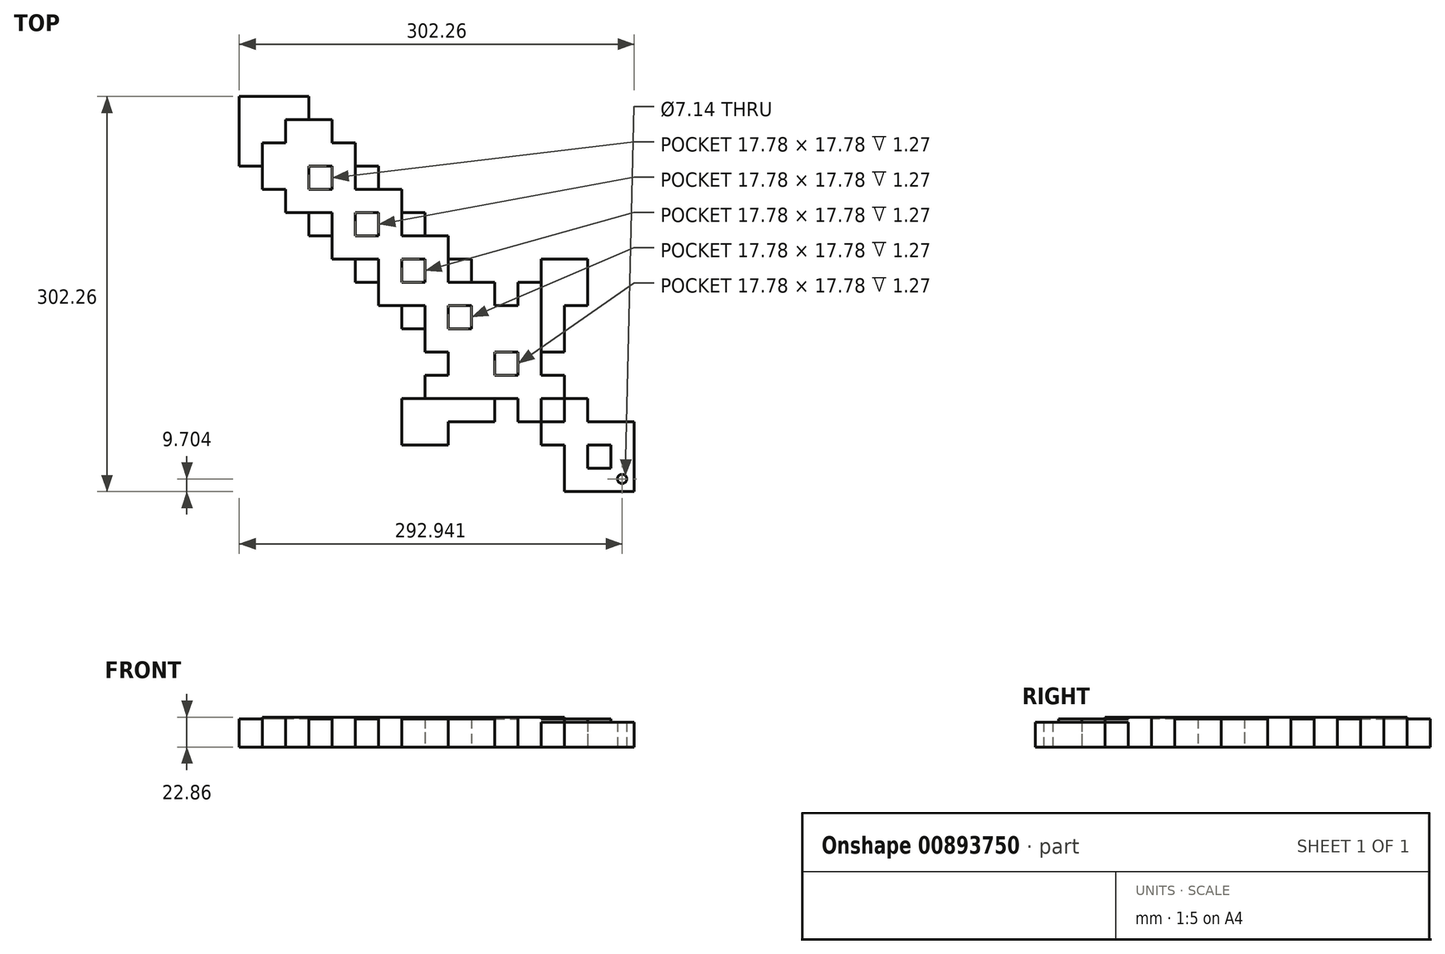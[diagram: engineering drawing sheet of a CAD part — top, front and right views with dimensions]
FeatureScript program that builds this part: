
annotation { "Feature Type Name" : "Feature", "Feature Type Description" : "" }
export const myFeature = defineFeature(function(context is Context, id is Id, definition is map)
    precondition{}
    {
        {
            var Q0;
            Q0=qCreatedBy(makeId("Top.planeOp"),FACE);
            var sketch = newSketch(context, id + "F0", { "sketchPlane" : qUnion([Q0])});
            skLineSegment(sketch, "E0.bottom", {"start": v(7.49, 0) * mm, "end": v(60.83, 0) * mm});
            skLineSegment(sketch, "E0.top", {"start": v(7.49, -53.34) * mm, "end": v(60.83, -53.34) * mm});
            skLineSegment(sketch, "E0.left", {"start": v(7.49, 0) * mm, "end": v(7.49, -53.34) * mm});
            skLineSegment(sketch, "E0.right", {"start": v(60.83, 0) * mm, "end": v(60.83, -53.34) * mm});
            skLineSegment(sketch, "E1.bottom", {"start": v(25.27, -17.78) * mm, "end": v(43.05, -17.78) * mm});
            skLineSegment(sketch, "E1.top", {"start": v(25.27, -35.56) * mm, "end": v(43.05, -35.56) * mm});
            skLineSegment(sketch, "E1.left", {"start": v(25.27, -17.78) * mm, "end": v(25.27, -35.56) * mm});
            skLineSegment(sketch, "E1.right", {"start": v(43.05, -17.78) * mm, "end": v(43.05, -35.56) * mm});
            skLineSegment(sketch, "E2.bottom", {"start": v(-10.3, 17.78) * mm, "end": v(25.27, 17.78) * mm});
            skLineSegment(sketch, "E2.top", {"start": v(-10.3, -17.78) * mm, "end": v(7.49, -17.78) * mm});
            skLineSegment(sketch, "E2.left", {"start": v(-10.3, 17.78) * mm, "end": v(-10.3, -17.78) * mm});
            skLineSegment(sketch, "E2.right", {"start": v(25.27, 17.78) * mm, "end": v(25.27, 0) * mm});
            skLineSegment(sketch, "E3.bottom", {"start": v(-10.3, 0) * mm, "end": v(-28.07, 0) * mm});
            skLineSegment(sketch, "E3.top", {"start": v(7.49, 35.56) * mm, "end": v(-28.07, 35.56) * mm});
            skLineSegment(sketch, "E3.left", {"start": v(7.49, 17.78) * mm, "end": v(7.49, 35.56) * mm});
            skLineSegment(sketch, "E3.right", {"start": v(-28.07, 0) * mm, "end": v(-28.07, 35.56) * mm});
            skLineSegment(sketch, "E4.bottom", {"start": v(-28.07, 17.78) * mm, "end": v(-45.85, 17.78) * mm});
            skLineSegment(sketch, "E4.top", {"start": v(-10.3, 53.34) * mm, "end": v(-45.85, 53.34) * mm});
            skLineSegment(sketch, "E4.left", {"start": v(-10.3, 35.56) * mm, "end": v(-10.3, 53.34) * mm});
            skLineSegment(sketch, "E4.right", {"start": v(-45.85, 17.78) * mm, "end": v(-45.85, 53.34) * mm});
            skLineSegment(sketch, "E5.bottom", {"start": v(-45.85, 53.34) * mm, "end": v(-10.3, 53.34) * mm});
            skLineSegment(sketch, "E5.top", {"start": v(-45.85, 88.9) * mm, "end": v(-10.3, 88.9) * mm});
            skLineSegment(sketch, "E5.left", {"start": v(-45.85, 53.34) * mm, "end": v(-45.85, 88.9) * mm});
            skLineSegment(sketch, "E5.right", {"start": v(-10.3, 53.34) * mm, "end": v(-10.3, 88.9) * mm});
            skPoint(sketch, "E6.oppositeSnap0", {"position": v(-36.96, 17.78) * mm});
            skLineSegment(sketch, "E6.bottom", {"start": v(-45.85, 53.34) * mm, "end": v(-81.41, 53.34) * mm});
            skLineSegment(sketch, "E6.top", {"start": v(-45.85, 17.78) * mm, "end": v(-81.41, 17.78) * mm});
            skLineSegment(sketch, "E6.left", {"start": v(-45.85, 53.34) * mm, "end": v(-45.85, 17.78) * mm});
            skLineSegment(sketch, "E6.right", {"start": v(-81.41, 53.34) * mm, "end": v(-81.41, 17.78) * mm});
            skLineSegment(sketch, "E7.bottom", {"start": v(-10.3, 88.9) * mm, "end": v(7.49, 88.9) * mm});
            skLineSegment(sketch, "E7.top", {"start": v(-10.3, 53.34) * mm, "end": v(7.49, 53.34) * mm});
            skLineSegment(sketch, "E7.left", {"start": v(-10.3, 88.9) * mm, "end": v(-10.3, 53.34) * mm});
            skLineSegment(sketch, "E7.right", {"start": v(7.49, 88.9) * mm, "end": v(7.49, 53.34) * mm});
            skLineSegment(sketch, "E8.right", {"start": v(-10.3, 88.9) * mm, "end": v(-10.3, 106.7) * mm});
            skLineSegment(sketch, "E9.bottom", {"start": v(-81.41, 17.78) * mm, "end": v(-99.41, 17.78) * mm});
            skLineSegment(sketch, "E9.left", {"start": v(-81.41, 17.78) * mm, "end": v(-81.41, 53.34) * mm});
            skLineSegment(sketch, "E10.bottom", {"start": v(-81.41, 17.78) * mm, "end": v(-45.85, 17.78) * mm});
            skLineSegment(sketch, "E10.top", {"start": v(-81.41, 0) * mm, "end": v(-45.85, 0) * mm});
            skLineSegment(sketch, "E10.left", {"start": v(-81.41, 17.78) * mm, "end": v(-81.41, 0) * mm});
            skLineSegment(sketch, "E10.right", {"start": v(-45.85, 17.78) * mm, "end": v(-45.85, 0) * mm});
            skLineSegment(sketch, "E11.bottom", {"start": v(-81.41, 17.78) * mm, "end": v(-116.97, 17.78) * mm});
            skLineSegment(sketch, "E11.top", {"start": v(-81.41, -17.78) * mm, "end": v(-116.97, -17.78) * mm});
            skLineSegment(sketch, "E11.left", {"start": v(-81.41, 17.78) * mm, "end": v(-81.41, -17.78) * mm});
            skLineSegment(sketch, "E11.right", {"start": v(-116.97, 17.78) * mm, "end": v(-116.97, -17.78) * mm});
            skLineSegment(sketch, "E12.bottom", {"start": v(-10.3, 88.9) * mm, "end": v(25.27, 88.9) * mm});
            skLineSegment(sketch, "E12.top", {"start": v(-10.3, 124.46) * mm, "end": v(25.27, 124.46) * mm});
            skLineSegment(sketch, "E12.left", {"start": v(-10.3, 88.9) * mm, "end": v(-10.3, 124.46) * mm});
            skLineSegment(sketch, "E12.right", {"start": v(25.27, 88.9) * mm, "end": v(25.27, 124.46) * mm});
            skLineSegment(sketch, "E13.top", {"start": v(-45.85, 88.9) * mm, "end": v(-81.41, 88.9) * mm});
            skLineSegment(sketch, "E13.right", {"start": v(-81.41, 53.34) * mm, "end": v(-81.41, 88.9) * mm});
            skPoint(sketch, "E14.end.orphan", {"position": v(-28.07, 88.9) * mm});
            skPoint(sketch, "E8.top.start.orphan", {"position": v(-28.3, 106.68) * mm});
            skPoint(sketch, "E15.end.orphan", {"position": v(-81.41, 35.56) * mm});
            skPoint(sketch, "E9.right.end.orphan", {"position": v(-99.41, 35.56) * mm});
            skLineSegment(sketch, "E16.bottom", {"start": v(-28.3, 106.68) * mm, "end": v(-10.3, 106.68) * mm});
            skLineSegment(sketch, "E16.top", {"start": v(-28.3, 88.9) * mm, "end": v(-10.3, 88.9) * mm});
            skLineSegment(sketch, "E16.left", {"start": v(-28.3, 106.68) * mm, "end": v(-28.3, 88.9) * mm});
            skLineSegment(sketch, "E16.right", {"start": v(-10.3, 106.68) * mm, "end": v(-10.3, 88.9) * mm});
            skLineSegment(sketch, "E17.bottom", {"start": v(-99.41, 35.56) * mm, "end": v(-81.41, 35.56) * mm});
            skLineSegment(sketch, "E17.top", {"start": v(-99.41, 17.78) * mm, "end": v(-81.41, 17.78) * mm});
            skLineSegment(sketch, "E17.left", {"start": v(-99.41, 35.56) * mm, "end": v(-99.41, 17.78) * mm});
            skLineSegment(sketch, "E17.right", {"start": v(-81.41, 35.56) * mm, "end": v(-81.41, 17.78) * mm});
            skLineSegment(sketch, "E18.bottom", {"start": v(-63.63, 71.12) * mm, "end": v(-99.2, 71.12) * mm});
            skLineSegment(sketch, "E18.top", {"start": v(-63.63, 106.68) * mm, "end": v(-99.2, 106.68) * mm});
            skLineSegment(sketch, "E18.left", {"start": v(-63.63, 71.12) * mm, "end": v(-63.63, 106.68) * mm});
            skLineSegment(sketch, "E18.right", {"start": v(-99.2, 71.12) * mm, "end": v(-99.2, 106.68) * mm});
            skLineSegment(sketch, "E19.bottom", {"start": v(-99.2, 88.9) * mm, "end": v(-116.97, 88.9) * mm});
            skLineSegment(sketch, "E19.top", {"start": v(-81.41, 124.46) * mm, "end": v(-116.97, 124.46) * mm});
            skLineSegment(sketch, "E19.left", {"start": v(-81.41, 106.68) * mm, "end": v(-81.41, 124.46) * mm});
            skLineSegment(sketch, "E19.right", {"start": v(-116.97, 88.9) * mm, "end": v(-116.97, 124.46) * mm});
            skLineSegment(sketch, "E20.bottom", {"start": v(-116.97, 106.68) * mm, "end": v(-134.75, 106.68) * mm});
            skLineSegment(sketch, "E20.top", {"start": v(-99.2, 142.24) * mm, "end": v(-134.75, 142.24) * mm});
            skLineSegment(sketch, "E20.left", {"start": v(-99.2, 124.46) * mm, "end": v(-99.2, 142.24) * mm});
            skLineSegment(sketch, "E20.right", {"start": v(-134.75, 106.68) * mm, "end": v(-134.75, 142.24) * mm});
            skLineSegment(sketch, "E21.bottom", {"start": v(-134.75, 124.46) * mm, "end": v(-152.53, 124.46) * mm});
            skLineSegment(sketch, "E21.top", {"start": v(-116.97, 160.02) * mm, "end": v(-152.53, 160.02) * mm});
            skLineSegment(sketch, "E21.left", {"start": v(-116.97, 142.24) * mm, "end": v(-116.97, 160.02) * mm});
            skLineSegment(sketch, "E21.right", {"start": v(-152.53, 124.46) * mm, "end": v(-152.53, 160.02) * mm});
            skLineSegment(sketch, "E22.bottom", {"start": v(-152.53, 142.24) * mm, "end": v(-170.31, 142.24) * mm});
            skLineSegment(sketch, "E22.top", {"start": v(-134.75, 177.8) * mm, "end": v(-170.31, 177.8) * mm});
            skLineSegment(sketch, "E22.left", {"start": v(-134.75, 160.02) * mm, "end": v(-134.75, 177.8) * mm});
            skLineSegment(sketch, "E22.right", {"start": v(-170.31, 142.24) * mm, "end": v(-170.31, 177.8) * mm});
            skLineSegment(sketch, "E23.bottom", {"start": v(-170.31, 160.02) * mm, "end": v(-188.1, 160.02) * mm});
            skLineSegment(sketch, "E23.top", {"start": v(-152.53, 195.58) * mm, "end": v(-188.1, 195.58) * mm});
            skLineSegment(sketch, "E23.left", {"start": v(-152.53, 177.8) * mm, "end": v(-152.53, 195.58) * mm});
            skLineSegment(sketch, "E23.right", {"start": v(-188.1, 160.02) * mm, "end": v(-188.1, 195.58) * mm});
            skLineSegment(sketch, "E24.bottom", {"start": v(-188.1, 177.8) * mm, "end": v(-205.87, 177.8) * mm});
            skLineSegment(sketch, "E24.top", {"start": v(-170.31, 213.36) * mm, "end": v(-205.87, 213.36) * mm});
            skLineSegment(sketch, "E24.left", {"start": v(-170.31, 195.58) * mm, "end": v(-170.31, 213.36) * mm});
            skLineSegment(sketch, "E24.right", {"start": v(-205.87, 177.8) * mm, "end": v(-205.87, 213.36) * mm});
            skLineSegment(sketch, "E25.bottom", {"start": v(-205.87, 195.58) * mm, "end": v(-223.65, 195.58) * mm});
            skLineSegment(sketch, "E25.top", {"start": v(-188.1, 231.14) * mm, "end": v(-223.65, 231.14) * mm});
            skLineSegment(sketch, "E25.left", {"start": v(-188.1, 213.36) * mm, "end": v(-188.1, 231.14) * mm});
            skLineSegment(sketch, "E25.right", {"start": v(-223.65, 195.58) * mm, "end": v(-223.65, 231.14) * mm});
            skLineSegment(sketch, "E26.top", {"start": v(-223.65, 195.58) * mm, "end": v(-241.43, 195.58) * mm});
            skLineSegment(sketch, "E26.right", {"start": v(-241.43, 231.14) * mm, "end": v(-241.43, 195.58) * mm});
            skLineSegment(sketch, "E27.top", {"start": v(-188.1, 248.92) * mm, "end": v(-223.65, 248.92) * mm});
            skLineSegment(sketch, "E27.left", {"start": v(-188.1, 231.14) * mm, "end": v(-188.1, 248.92) * mm});
            skLineSegment(sketch, "E28.top", {"start": v(-223.65, 248.92) * mm, "end": v(-241.43, 248.92) * mm});
            skLineSegment(sketch, "E28.right", {"start": v(-241.43, 231.14) * mm, "end": v(-241.43, 248.92) * mm});
            skLineSegment(sketch, "E29.bottom", {"start": v(-63.63, 106.68) * mm, "end": v(-45.85, 106.68) * mm});
            skLineSegment(sketch, "E29.top", {"start": v(-63.63, 88.9) * mm, "end": v(-45.85, 88.9) * mm});
            skLineSegment(sketch, "E29.left", {"start": v(-63.63, 106.68) * mm, "end": v(-63.63, 88.9) * mm});
            skLineSegment(sketch, "E29.right", {"start": v(-45.85, 106.68) * mm, "end": v(-45.85, 88.9) * mm});
            skLineSegment(sketch, "E30.bottom", {"start": v(-99.2, 71.12) * mm, "end": v(-81.41, 71.12) * mm});
            skLineSegment(sketch, "E30.top", {"start": v(-99.2, 53.34) * mm, "end": v(-81.41, 53.34) * mm});
            skLineSegment(sketch, "E30.left", {"start": v(-99.2, 71.12) * mm, "end": v(-99.2, 53.34) * mm});
            skLineSegment(sketch, "E30.right", {"start": v(-81.41, 71.12) * mm, "end": v(-81.41, 53.34) * mm});
            skLineSegment(sketch, "E31.bottom", {"start": v(-223.65, 195.58) * mm, "end": v(-205.87, 195.58) * mm});
            skLineSegment(sketch, "E31.top", {"start": v(-223.65, 177.8) * mm, "end": v(-205.87, 177.8) * mm});
            skLineSegment(sketch, "E31.left", {"start": v(-223.65, 195.58) * mm, "end": v(-223.65, 177.8) * mm});
            skLineSegment(sketch, "E31.right", {"start": v(-205.87, 195.58) * mm, "end": v(-205.87, 177.8) * mm});
            skLineSegment(sketch, "E32.bottom", {"start": v(-205.87, 177.8) * mm, "end": v(-188.1, 177.8) * mm});
            skLineSegment(sketch, "E32.top", {"start": v(-205.87, 160.02) * mm, "end": v(-188.1, 160.02) * mm});
            skLineSegment(sketch, "E32.left", {"start": v(-205.87, 177.8) * mm, "end": v(-205.87, 160.02) * mm});
            skLineSegment(sketch, "E32.right", {"start": v(-188.1, 177.8) * mm, "end": v(-188.1, 160.02) * mm});
            skLineSegment(sketch, "E33.bottom", {"start": v(-188.1, 160.02) * mm, "end": v(-170.31, 160.02) * mm});
            skLineSegment(sketch, "E33.top", {"start": v(-188.1, 142.24) * mm, "end": v(-170.31, 142.24) * mm});
            skLineSegment(sketch, "E33.left", {"start": v(-188.1, 160.02) * mm, "end": v(-188.1, 142.24) * mm});
            skLineSegment(sketch, "E33.right", {"start": v(-170.31, 160.02) * mm, "end": v(-170.31, 142.24) * mm});
            skLineSegment(sketch, "E34.bottom", {"start": v(-170.31, 142.24) * mm, "end": v(-152.53, 142.24) * mm});
            skLineSegment(sketch, "E34.top", {"start": v(-170.31, 124.46) * mm, "end": v(-152.53, 124.46) * mm});
            skLineSegment(sketch, "E34.left", {"start": v(-170.31, 142.24) * mm, "end": v(-170.31, 124.46) * mm});
            skLineSegment(sketch, "E34.right", {"start": v(-152.53, 142.24) * mm, "end": v(-152.53, 124.46) * mm});
            skLineSegment(sketch, "E35.bottom", {"start": v(-152.53, 124.46) * mm, "end": v(-134.75, 124.46) * mm});
            skLineSegment(sketch, "E35.top", {"start": v(-152.53, 106.68) * mm, "end": v(-134.75, 106.68) * mm});
            skLineSegment(sketch, "E35.left", {"start": v(-152.53, 124.46) * mm, "end": v(-152.53, 106.68) * mm});
            skLineSegment(sketch, "E35.right", {"start": v(-134.75, 124.46) * mm, "end": v(-134.75, 106.68) * mm});
            skLineSegment(sketch, "E36.bottom", {"start": v(-134.75, 106.68) * mm, "end": v(-116.97, 106.68) * mm});
            skLineSegment(sketch, "E36.top", {"start": v(-134.75, 88.9) * mm, "end": v(-116.97, 88.9) * mm});
            skLineSegment(sketch, "E36.left", {"start": v(-134.75, 106.68) * mm, "end": v(-134.75, 88.9) * mm});
            skLineSegment(sketch, "E36.right", {"start": v(-116.97, 106.68) * mm, "end": v(-116.97, 88.9) * mm});
            skLineSegment(sketch, "E37.bottom", {"start": v(-116.97, 88.9) * mm, "end": v(-99.2, 88.9) * mm});
            skLineSegment(sketch, "E37.top", {"start": v(-116.97, 71.12) * mm, "end": v(-99.2, 71.12) * mm});
            skLineSegment(sketch, "E37.left", {"start": v(-116.97, 88.9) * mm, "end": v(-116.97, 71.12) * mm});
            skLineSegment(sketch, "E37.right", {"start": v(-99.2, 88.9) * mm, "end": v(-99.2, 71.12) * mm});
            skLineSegment(sketch, "E38.bottom", {"start": v(-188.1, 231.14) * mm, "end": v(-170.31, 231.14) * mm});
            skLineSegment(sketch, "E38.top", {"start": v(-188.1, 213.36) * mm, "end": v(-170.31, 213.36) * mm});
            skLineSegment(sketch, "E38.left", {"start": v(-188.1, 231.14) * mm, "end": v(-188.1, 213.36) * mm});
            skLineSegment(sketch, "E38.right", {"start": v(-170.31, 231.14) * mm, "end": v(-170.31, 213.36) * mm});
            skLineSegment(sketch, "E39.bottom", {"start": v(-170.31, 213.36) * mm, "end": v(-152.53, 213.36) * mm});
            skLineSegment(sketch, "E39.top", {"start": v(-170.31, 195.58) * mm, "end": v(-152.53, 195.58) * mm});
            skLineSegment(sketch, "E39.left", {"start": v(-170.31, 213.36) * mm, "end": v(-170.31, 195.58) * mm});
            skLineSegment(sketch, "E39.right", {"start": v(-152.53, 213.36) * mm, "end": v(-152.53, 195.58) * mm});
            skLineSegment(sketch, "E40.bottom", {"start": v(-152.53, 195.58) * mm, "end": v(-134.75, 195.58) * mm});
            skLineSegment(sketch, "E40.top", {"start": v(-152.53, 177.8) * mm, "end": v(-134.75, 177.8) * mm});
            skLineSegment(sketch, "E40.left", {"start": v(-152.53, 195.58) * mm, "end": v(-152.53, 177.8) * mm});
            skLineSegment(sketch, "E40.right", {"start": v(-134.75, 195.58) * mm, "end": v(-134.75, 177.8) * mm});
            skLineSegment(sketch, "E41.bottom", {"start": v(-134.75, 177.8) * mm, "end": v(-116.97, 177.8) * mm});
            skLineSegment(sketch, "E41.top", {"start": v(-134.75, 160.02) * mm, "end": v(-116.97, 160.02) * mm});
            skLineSegment(sketch, "E41.left", {"start": v(-134.75, 177.8) * mm, "end": v(-134.75, 160.02) * mm});
            skLineSegment(sketch, "E41.right", {"start": v(-116.97, 177.8) * mm, "end": v(-116.97, 160.02) * mm});
            skLineSegment(sketch, "E42.bottom", {"start": v(-116.97, 160.02) * mm, "end": v(-99.2, 160.02) * mm});
            skLineSegment(sketch, "E42.top", {"start": v(-116.97, 142.24) * mm, "end": v(-99.2, 142.24) * mm});
            skLineSegment(sketch, "E42.left", {"start": v(-116.97, 160.02) * mm, "end": v(-116.97, 142.24) * mm});
            skLineSegment(sketch, "E42.right", {"start": v(-99.2, 160.02) * mm, "end": v(-99.2, 142.24) * mm});
            skLineSegment(sketch, "E43.bottom", {"start": v(-99.2, 142.24) * mm, "end": v(-81.41, 142.24) * mm});
            skLineSegment(sketch, "E43.top", {"start": v(-99.2, 124.46) * mm, "end": v(-81.41, 124.46) * mm});
            skLineSegment(sketch, "E43.left", {"start": v(-99.2, 142.24) * mm, "end": v(-99.2, 124.46) * mm});
            skLineSegment(sketch, "E43.right", {"start": v(-81.41, 142.24) * mm, "end": v(-81.41, 124.46) * mm});
            skLineSegment(sketch, "E44.bottom", {"start": v(-81.41, 124.46) * mm, "end": v(-63.63, 124.46) * mm});
            skLineSegment(sketch, "E44.top", {"start": v(-81.41, 106.68) * mm, "end": v(-63.63, 106.68) * mm});
            skLineSegment(sketch, "E44.left", {"start": v(-81.41, 124.46) * mm, "end": v(-81.41, 106.68) * mm});
            skLineSegment(sketch, "E44.right", {"start": v(-63.63, 124.46) * mm, "end": v(-63.63, 106.68) * mm});
            skLineSegment(sketch, "E45.top", {"start": v(-99.41, 0) * mm, "end": v(-81.41, 0) * mm});
            skLineSegment(sketch, "E45.left", {"start": v(-99.41, 17.78) * mm, "end": v(-99.41, 0) * mm});
            skLineSegment(sketch, "E46.bottom", {"start": v(-10.3, 106.7) * mm, "end": v(7.49, 106.7) * mm});
            skLineSegment(sketch, "E46.left", {"start": v(-10.3, 106.7) * mm, "end": v(-10.3, 88.9) * mm});
            skLineSegment(sketch, "E46.right", {"start": v(7.49, 106.7) * mm, "end": v(7.49, 88.9) * mm});
            skLineSegment(sketch, "E47.top", {"start": v(-81.41, 35.56) * mm, "end": v(-45.85, 35.56) * mm});
            skLineSegment(sketch, "E47.left", {"start": v(-81.41, 17.78) * mm, "end": v(-81.41, 35.56) * mm});
            skLineSegment(sketch, "E47.right", {"start": v(-45.85, 17.78) * mm, "end": v(-45.85, 35.56) * mm});
            skLineSegment(sketch, "E48.bottom", {"start": v(-28.07, 88.9) * mm, "end": v(-10.3, 88.9) * mm});
            skLineSegment(sketch, "E48.top", {"start": v(-28.07, 53.34) * mm, "end": v(-10.3, 53.34) * mm});
            skLineSegment(sketch, "E48.left", {"start": v(-28.07, 88.9) * mm, "end": v(-28.07, 53.34) * mm});
            skLineSegment(sketch, "E49.bottom", {"start": v(-45.85, 53.34) * mm, "end": v(-28.07, 53.34) * mm});
            skLineSegment(sketch, "E49.top", {"start": v(-45.85, 35.56) * mm, "end": v(-28.07, 35.56) * mm});
            skLineSegment(sketch, "E49.left", {"start": v(-45.85, 53.34) * mm, "end": v(-45.85, 35.56) * mm});
            skLineSegment(sketch, "E49.right", {"start": v(-28.07, 53.34) * mm, "end": v(-28.07, 35.56) * mm});
            skLineSegment(sketch, "E50.bottom", {"start": v(25.27, -17.78) * mm, "end": v(7.49, -17.78) * mm});
            skLineSegment(sketch, "E50.top", {"start": v(25.27, 0) * mm, "end": v(7.49, 0) * mm});
            skLineSegment(sketch, "E50.left", {"start": v(25.27, -17.78) * mm, "end": v(25.27, 0) * mm});
            skLineSegment(sketch, "E50.right", {"start": v(7.49, -17.78) * mm, "end": v(7.49, 0) * mm});
            skLineSegment(sketch, "E51.bottom", {"start": v(7.49, 0) * mm, "end": v(-10.3, 0) * mm});
            skLineSegment(sketch, "E51.top", {"start": v(7.49, 17.78) * mm, "end": v(-10.3, 17.78) * mm});
            skLineSegment(sketch, "E51.left", {"start": v(7.49, 0) * mm, "end": v(7.49, 17.78) * mm});
            skLineSegment(sketch, "E51.right", {"start": v(-10.3, 0) * mm, "end": v(-10.3, 17.78) * mm});
            skLineSegment(sketch, "E52.bottom", {"start": v(-10.14, 17.95) * mm, "end": v(-28.07, 17.95) * mm});
            skLineSegment(sketch, "E52.top", {"start": v(-10.14, 35.56) * mm, "end": v(-28.07, 35.56) * mm});
            skLineSegment(sketch, "E52.left", {"start": v(-10.14, 17.95) * mm, "end": v(-10.14, 35.56) * mm});
            skLineSegment(sketch, "E52.right", {"start": v(-28.07, 17.95) * mm, "end": v(-28.07, 35.56) * mm});
            skLineSegment(sketch, "E53.bottom", {"start": v(-45.85, 53.34) * mm, "end": v(-63.63, 53.34) * mm});
            skLineSegment(sketch, "E53.top", {"start": v(-45.85, 71.12) * mm, "end": v(-63.63, 71.12) * mm});
            skLineSegment(sketch, "E53.left", {"start": v(-45.85, 53.34) * mm, "end": v(-45.85, 71.12) * mm});
            skLineSegment(sketch, "E53.right", {"start": v(-63.63, 53.34) * mm, "end": v(-63.63, 71.12) * mm});
            skLineSegment(sketch, "E54.bottom", {"start": v(-81.41, 88.9) * mm, "end": v(-99.2, 88.9) * mm});
            skLineSegment(sketch, "E54.top", {"start": v(-81.41, 106.68) * mm, "end": v(-99.2, 106.68) * mm});
            skLineSegment(sketch, "E54.left", {"start": v(-81.41, 88.9) * mm, "end": v(-81.41, 106.68) * mm});
            skLineSegment(sketch, "E54.right", {"start": v(-99.2, 88.9) * mm, "end": v(-99.2, 106.68) * mm});
            skLineSegment(sketch, "E55.bottom", {"start": v(-99.2, 106.68) * mm, "end": v(-116.97, 106.68) * mm});
            skLineSegment(sketch, "E55.top", {"start": v(-99.2, 124.46) * mm, "end": v(-116.97, 124.46) * mm});
            skLineSegment(sketch, "E55.left", {"start": v(-99.2, 106.68) * mm, "end": v(-99.2, 124.46) * mm});
            skLineSegment(sketch, "E55.right", {"start": v(-116.97, 106.68) * mm, "end": v(-116.97, 124.46) * mm});
            skLineSegment(sketch, "E56.bottom", {"start": v(-117.55, 124.26) * mm, "end": v(-134.75, 124.26) * mm});
            skLineSegment(sketch, "E56.top", {"start": v(-117.55, 142.24) * mm, "end": v(-134.75, 142.24) * mm});
            skLineSegment(sketch, "E56.left", {"start": v(-117.55, 124.26) * mm, "end": v(-117.55, 142.24) * mm});
            skLineSegment(sketch, "E56.right", {"start": v(-134.75, 124.26) * mm, "end": v(-134.75, 142.24) * mm});
            skLineSegment(sketch, "E57.bottom", {"start": v(-134.75, 142.24) * mm, "end": v(-152.53, 142.24) * mm});
            skLineSegment(sketch, "E57.top", {"start": v(-134.75, 160.02) * mm, "end": v(-152.53, 160.02) * mm});
            skLineSegment(sketch, "E57.left", {"start": v(-134.75, 142.24) * mm, "end": v(-134.75, 160.02) * mm});
            skLineSegment(sketch, "E57.right", {"start": v(-152.53, 142.24) * mm, "end": v(-152.53, 160.02) * mm});
            skLineSegment(sketch, "E58.bottom", {"start": v(-152.53, 160.02) * mm, "end": v(-170.31, 160.02) * mm});
            skLineSegment(sketch, "E58.top", {"start": v(-152.53, 177.8) * mm, "end": v(-170.31, 177.8) * mm});
            skLineSegment(sketch, "E58.left", {"start": v(-152.53, 160.02) * mm, "end": v(-152.53, 177.8) * mm});
            skLineSegment(sketch, "E58.right", {"start": v(-170.31, 160.02) * mm, "end": v(-170.31, 177.8) * mm});
            skLineSegment(sketch, "E59.bottom", {"start": v(-170.31, 177.8) * mm, "end": v(-188.1, 177.8) * mm});
            skLineSegment(sketch, "E59.top", {"start": v(-170.31, 195.58) * mm, "end": v(-188.1, 195.58) * mm});
            skLineSegment(sketch, "E59.left", {"start": v(-170.31, 177.8) * mm, "end": v(-170.31, 195.58) * mm});
            skLineSegment(sketch, "E59.right", {"start": v(-188.1, 177.8) * mm, "end": v(-188.1, 195.58) * mm});
            skLineSegment(sketch, "E60.bottom", {"start": v(-188.1, 195.58) * mm, "end": v(-205.87, 195.58) * mm});
            skLineSegment(sketch, "E60.top", {"start": v(-188.1, 213.36) * mm, "end": v(-205.87, 213.36) * mm});
            skLineSegment(sketch, "E60.left", {"start": v(-188.1, 195.58) * mm, "end": v(-188.1, 213.36) * mm});
            skLineSegment(sketch, "E60.right", {"start": v(-205.87, 195.58) * mm, "end": v(-205.87, 213.36) * mm});
            skLineSegment(sketch, "E61.bottom", {"start": v(-205.87, 213.36) * mm, "end": v(-223.65, 213.36) * mm});
            skLineSegment(sketch, "E61.top", {"start": v(-205.87, 231.14) * mm, "end": v(-223.65, 231.14) * mm});
            skLineSegment(sketch, "E61.left", {"start": v(-205.87, 213.36) * mm, "end": v(-205.87, 231.14) * mm});
            skLineSegment(sketch, "E61.right", {"start": v(-223.65, 213.36) * mm, "end": v(-223.65, 231.14) * mm});
            skPoint(sketch, "E62", {"position": v(51.51, -43.64) * mm});
            skSolve(sketch);
        }
        {
            var Q0;
            {var subQ0=sQuery(id+"F0.wireOp",EDGE,"E56.bottom");Q0=makeQuery(id+"F0.imprint","IMPRINT",FACE,{"disambiguationData":[TD([[makeQuery(id+"F0.imprint","IMPRINT",EDGE,{"derivedFrom":subQ0}),-1.0]])]});}
            var Q1;
            {var subQ2=sQuery(id+"F0.wireOp",EDGE,"E22.bottom");Q1=makeQuery(id+"F0.imprint","IMPRINT",FACE,{"disambiguationData":[TD([[makeQuery(id+"F0.imprint","IMPRINT",EDGE,{"derivedFrom":subQ2}),-1.0]])]});}
            var Q2;
            {var subQ0=sQuery(id+"F0.wireOp",EDGE,"E6.top");Q2=makeQuery(id+"F0.imprint","IMPRINT",FACE,{"disambiguationData":[TD([[makeQuery(id+"F0.imprint","IMPRINT",EDGE,{"derivedFrom":subQ0}),-1.0]])]});}
            var Q3;
            {var subQ2=sQuery(id+"F0.wireOp",EDGE,"E23.bottom");Q3=makeQuery(id+"F0.imprint","IMPRINT",FACE,{"disambiguationData":[TD([[makeQuery(id+"F0.imprint","IMPRINT",EDGE,{"derivedFrom":subQ2}),-1.0]])]});}
            var Q4;
            {var subQ2=sQuery(id+"F0.wireOp",EDGE,"E20.left");Q4=makeQuery(id+"F0.imprint","IMPRINT",FACE,{"disambiguationData":[TD([[makeQuery(id+"F0.imprint","IMPRINT",EDGE,{"derivedFrom":subQ2}),-1.0]])]});}
            var Q5;
            {var subQ3=sQuery(id+"F0.wireOp",EDGE,"E7.bottom");Q5=makeQuery(id+"F0.imprint","IMPRINT",FACE,{"disambiguationData":[TD([[makeQuery(id+"F0.imprint","IMPRINT",EDGE,{"derivedFrom":subQ3}),1.0]])]});}
            var Q6;
            {var subQ0=sQuery(id+"F0.wireOp",EDGE,"E54.left");Q6=makeQuery(id+"F0.imprint","IMPRINT",FACE,{"disambiguationData":[TD([[makeQuery(id+"F0.imprint","IMPRINT",EDGE,{"derivedFrom":subQ0}),-1.0]])]});}
            var Q7;
            {var subQ4=sQuery(id+"F0.wireOp",EDGE,"E50.bottom");Q7=makeQuery(id+"F0.imprint","IMPRINT",FACE,{"disambiguationData":[TD([[makeQuery(id+"F0.imprint","IMPRINT",EDGE,{"derivedFrom":subQ4}),-1.0]])]});}
            var Q8;
            {var subQ0=sQuery(id+"F0.wireOp",EDGE,"E9.bottom");Q8=makeQuery(id+"F0.imprint","IMPRINT",FACE,{"disambiguationData":[TD([[makeQuery(id+"F0.imprint","IMPRINT",EDGE,{"derivedFrom":subQ0}),-1.0]])]});}
            var Q9;
            {var subQ0=sQuery(id+"F0.wireOp",EDGE,"E19.left");Q9=makeQuery(id+"F0.imprint","IMPRINT",FACE,{"disambiguationData":[TD([[makeQuery(id+"F0.imprint","IMPRINT",EDGE,{"derivedFrom":subQ0}),-1.0]])]});}
            var Q10;
            {var subQ0=sQuery(id+"F0.wireOp",EDGE,"E4.left");Q10=makeQuery(id+"F0.imprint","IMPRINT",FACE,{"disambiguationData":[TD([[makeQuery(id+"F0.imprint","IMPRINT",EDGE,{"derivedFrom":subQ0}),1.0]])]});}
            var Q11;
            {var subQ4=sQuery(id+"F0.wireOp",EDGE,"E57.bottom");Q11=makeQuery(id+"F0.imprint","IMPRINT",FACE,{"disambiguationData":[TD([[makeQuery(id+"F0.imprint","IMPRINT",EDGE,{"derivedFrom":subQ4}),-1.0]])]});}
            var Q12;
            {var subQ0=sQuery(id+"F0.wireOp",EDGE,"E23.left");Q12=makeQuery(id+"F0.imprint","IMPRINT",FACE,{"disambiguationData":[TD([[makeQuery(id+"F0.imprint","IMPRINT",EDGE,{"derivedFrom":subQ0}),-1.0]])]});}
            var Q13;
            {var subQ2=sQuery(id+"F0.wireOp",EDGE,"E21.left");Q13=makeQuery(id+"F0.imprint","IMPRINT",FACE,{"disambiguationData":[TD([[makeQuery(id+"F0.imprint","IMPRINT",EDGE,{"derivedFrom":subQ2}),-1.0]])]});}
            var Q14;
            {var subQ0=sQuery(id+"F0.wireOp",EDGE,"E2.top");Q14=makeQuery(id+"F0.imprint","IMPRINT",FACE,{"disambiguationData":[TD([[makeQuery(id+"F0.imprint","IMPRINT",EDGE,{"derivedFrom":subQ0}),1.0]])]});}
            var Q15;
            {var subQ1=sQuery(id+"F0.wireOp",EDGE,"E0.top");Q15=makeQuery(id+"F0.imprint","IMPRINT",FACE,{"disambiguationData":[TD([[makeQuery(id+"F0.imprint","IMPRINT",EDGE,{"derivedFrom":subQ1}),1.0]])]});}
            var Q16;
            {var subQ2=sQuery(id+"F0.wireOp",EDGE,"E22.bottom");Q16=makeQuery(id+"F0.imprint","IMPRINT",FACE,{"disambiguationData":[TD([[makeQuery(id+"F0.imprint","IMPRINT",EDGE,{"derivedFrom":subQ2}),1.0]])]});}
            var Q17;
            {var subQ4=sQuery(id+"F0.wireOp",EDGE,"E55.bottom");Q17=makeQuery(id+"F0.imprint","IMPRINT",FACE,{"disambiguationData":[TD([[makeQuery(id+"F0.imprint","IMPRINT",EDGE,{"derivedFrom":subQ4}),-1.0]])]});}
            var Q18;
            {var subQ3=sQuery(id+"F0.wireOp",EDGE,"E3.bottom");Q18=makeQuery(id+"F0.imprint","IMPRINT",FACE,{"disambiguationData":[TD([[makeQuery(id+"F0.imprint","IMPRINT",EDGE,{"derivedFrom":subQ3}),-1.0]])]});}
            var Q19;
            {var subQ0=sQuery(id+"F0.wireOp",EDGE,"E30.top");Q19=makeQuery(id+"F0.imprint","IMPRINT",FACE,{"disambiguationData":[TD([[makeQuery(id+"F0.imprint","IMPRINT",EDGE,{"derivedFrom":subQ0}),1.0]])]});}
            var Q20;
            {var subQ0=sQuery(id+"F0.wireOp",EDGE,"E24.left");Q20=makeQuery(id+"F0.imprint","IMPRINT",FACE,{"disambiguationData":[TD([[makeQuery(id+"F0.imprint","IMPRINT",EDGE,{"derivedFrom":subQ0}),-1.0]])]});}
            var Q21;
            {var subQ0=sQuery(id+"F0.wireOp",EDGE,"E52.bottom");Q21=makeQuery(id+"F0.imprint","IMPRINT",FACE,{"disambiguationData":[TD([[makeQuery(id+"F0.imprint","IMPRINT",EDGE,{"derivedFrom":subQ0}),-1.0]])]});}
            var Q22;
            {var subQ0=sQuery(id+"F0.wireOp",EDGE,"E53.top");Q22=makeQuery(id+"F0.imprint","IMPRINT",FACE,{"disambiguationData":[TD([[makeQuery(id+"F0.imprint","IMPRINT",EDGE,{"derivedFrom":subQ0}),-1.0]])]});}
            var Q23;
            {var subQ2=sQuery(id+"F0.wireOp",EDGE,"E24.bottom");Q23=makeQuery(id+"F0.imprint","IMPRINT",FACE,{"disambiguationData":[TD([[makeQuery(id+"F0.imprint","IMPRINT",EDGE,{"derivedFrom":subQ2}),1.0]])]});}
            var Q24;
            {var subQ2=sQuery(id+"F0.wireOp",EDGE,"E22.left");Q24=makeQuery(id+"F0.imprint","IMPRINT",FACE,{"disambiguationData":[TD([[makeQuery(id+"F0.imprint","IMPRINT",EDGE,{"derivedFrom":subQ2}),1.0]])]});}
            var Q25;
            {var subQ0=sQuery(id+"F0.wireOp",EDGE,"E19.bottom");Q25=makeQuery(id+"F0.imprint","IMPRINT",FACE,{"disambiguationData":[TD([[makeQuery(id+"F0.imprint","IMPRINT",EDGE,{"derivedFrom":subQ0}),1.0]])]});}
            var Q26;
            {var subQ4=sQuery(id+"F0.wireOp",EDGE,"E58.bottom");Q26=makeQuery(id+"F0.imprint","IMPRINT",FACE,{"disambiguationData":[TD([[makeQuery(id+"F0.imprint","IMPRINT",EDGE,{"derivedFrom":subQ4}),-1.0]])]});}
            var Q27;
            {var subQ4=sQuery(id+"F0.wireOp",EDGE,"E59.bottom");Q27=makeQuery(id+"F0.imprint","IMPRINT",FACE,{"disambiguationData":[TD([[makeQuery(id+"F0.imprint","IMPRINT",EDGE,{"derivedFrom":subQ4}),-1.0]])]});}
            var Q28;
            {var subQ0=sQuery(id+"F0.wireOp",EDGE,"E21.bottom");Q28=makeQuery(id+"F0.imprint","IMPRINT",FACE,{"disambiguationData":[TD([[makeQuery(id+"F0.imprint","IMPRINT",EDGE,{"derivedFrom":subQ0}),-1.0]])]});}
            var Q29;
            Q29=makeQuery(id+"F0.imprint","IMPRINT",FACE,{"disambiguationData":[TD([[makeQuery(id+"F0.imprint","IMPRINT",EDGE,{"derivedFrom":sQuery(id+"F0.wireOp",EDGE,"E9.bottom")}),1.0]])]});
            var Q30;
            {var subQ0=sQuery(id+"F0.wireOp",EDGE,"E4.bottom");Q30=makeQuery(id+"F0.imprint","IMPRINT",FACE,{"disambiguationData":[TD([[makeQuery(id+"F0.imprint","IMPRINT",EDGE,{"derivedFrom":subQ0}),-1.0]])]});}
            var Q31;
            {var subQ4=sQuery(id+"F0.wireOp",EDGE,"E29.bottom");Q31=makeQuery(id+"F0.imprint","IMPRINT",FACE,{"disambiguationData":[TD([[makeQuery(id+"F0.imprint","IMPRINT",EDGE,{"derivedFrom":subQ4}),-1.0]])]});}
            var Q32;
            {var subQ3=sQuery(id+"F0.wireOp",EDGE,"E53.right");Q32=makeQuery(id+"F0.imprint","IMPRINT",FACE,{"disambiguationData":[TD([[makeQuery(id+"F0.imprint","IMPRINT",EDGE,{"derivedFrom":subQ3}),1.0]])]});}
            var Q33;
            {var subQ4=sQuery(id+"F0.wireOp",EDGE,"E60.bottom");Q33=makeQuery(id+"F0.imprint","IMPRINT",FACE,{"disambiguationData":[TD([[makeQuery(id+"F0.imprint","IMPRINT",EDGE,{"derivedFrom":subQ4}),-1.0]])]});}
            var Q34;
            Q34=makeQuery(id+"F0.imprint","IMPRINT",FACE,{"disambiguationData":[TD([[makeQuery(id+"F0.imprint","IMPRINT",EDGE,{"derivedFrom":sQuery(id+"F0.wireOp",EDGE,"E1.bottom")}),-1.0]])]});
            var Q35;
            Q35=makeQuery(id+"F0.imprint","IMPRINT",FACE,{"disambiguationData":[TD([[makeQuery(id+"F0.imprint","IMPRINT",EDGE,{"derivedFrom":sQuery(id+"F0.wireOp",EDGE,"E6.top")}),1.0]])]});
            var Q36;
            {var subQ4=sQuery(id+"F0.wireOp",EDGE,"E61.bottom");Q36=makeQuery(id+"F0.imprint","IMPRINT",FACE,{"disambiguationData":[TD([[makeQuery(id+"F0.imprint","IMPRINT",EDGE,{"derivedFrom":subQ4}),-1.0]])]});}
            var Q37;
            {var subQ1=sQuery(id+"F0.wireOp",EDGE,"E13.top");var subQ3=sQuery(id+"F0.wireOp",EDGE,"E18.left");var subQ4=makeQuery(id+"F0.imprint","INTERSECT",VERTEX,{"derivedFrom":[subQ1,subQ3]});Q37=makeQuery(id+"F0.imprint","IMPRINT",FACE,{"disambiguationData":[TD([[makeQuery(id+"F0.imprint","IMPRINT",EDGE,{"disambiguationData":[TD([[subQ4,-1.0]])],"derivedFrom":subQ1}),1.0]])]});}
            var Q38;
            {var subQ2=sQuery(id+"F0.wireOp",EDGE,"E25.left");Q38=makeQuery(id+"F0.imprint","IMPRINT",FACE,{"disambiguationData":[TD([[makeQuery(id+"F0.imprint","IMPRINT",EDGE,{"derivedFrom":subQ2}),-1.0]])]});}
            var Q39;
            {var subQ0=sQuery(id+"F0.wireOp",EDGE,"E21.bottom");Q39=makeQuery(id+"F0.imprint","IMPRINT",FACE,{"disambiguationData":[TD([[makeQuery(id+"F0.imprint","IMPRINT",EDGE,{"derivedFrom":subQ0}),1.0]])]});}
            var Q40;
            {var subQ0=sQuery(id+"F0.wireOp",EDGE,"E23.left");Q40=makeQuery(id+"F0.imprint","IMPRINT",FACE,{"disambiguationData":[TD([[makeQuery(id+"F0.imprint","IMPRINT",EDGE,{"derivedFrom":subQ0}),1.0]])]});}
            var Q41;
            Q41=makeQuery(id+"F0.imprint","IMPRINT",FACE,{"disambiguationData":[TD([[makeQuery(id+"F0.imprint","IMPRINT",EDGE,{"derivedFrom":sQuery(id+"F0.wireOp",EDGE,"E5.right")}),-1.0]])]});
            var Q42;
            {var subQ2=sQuery(id+"F0.wireOp",EDGE,"E20.bottom");Q42=makeQuery(id+"F0.imprint","IMPRINT",FACE,{"disambiguationData":[TD([[makeQuery(id+"F0.imprint","IMPRINT",EDGE,{"derivedFrom":subQ2}),1.0]])]});}
            var Q43;
            {var subQ0=sQuery(id+"F0.wireOp",EDGE,"E19.left");Q43=makeQuery(id+"F0.imprint","IMPRINT",FACE,{"disambiguationData":[TD([[makeQuery(id+"F0.imprint","IMPRINT",EDGE,{"derivedFrom":subQ0}),1.0]])]});}
            var Q44;
            {var subQ4=sQuery(id+"F0.wireOp",EDGE,"E51.bottom");Q44=makeQuery(id+"F0.imprint","IMPRINT",FACE,{"disambiguationData":[TD([[makeQuery(id+"F0.imprint","IMPRINT",EDGE,{"derivedFrom":subQ4}),-1.0]])]});}
            var Q45;
            {var subQ4=sQuery(id+"F0.wireOp",EDGE,"E54.bottom");Q45=makeQuery(id+"F0.imprint","IMPRINT",FACE,{"disambiguationData":[TD([[makeQuery(id+"F0.imprint","IMPRINT",EDGE,{"derivedFrom":subQ4}),-1.0]])]});}
            var Q46;
            Q46=makeQuery(id+"F0.imprint","IMPRINT",FACE,{"disambiguationData":[TD([[makeQuery(id+"F0.imprint","IMPRINT",EDGE,{"derivedFrom":sQuery(id+"F0.wireOp",EDGE,"E11.bottom")}),1.0]])]});
            var Q47;
            {var subQ3=sQuery(id+"F0.wireOp",EDGE,"E16.bottom");Q47=makeQuery(id+"F0.imprint","IMPRINT",FACE,{"disambiguationData":[TD([[makeQuery(id+"F0.imprint","IMPRINT",EDGE,{"derivedFrom":subQ3}),-1.0]])]});}
            var Q48;
            {var subQ2=sQuery(id+"F0.wireOp",EDGE,"E25.left");Q48=makeQuery(id+"F0.imprint","IMPRINT",FACE,{"disambiguationData":[TD([[makeQuery(id+"F0.imprint","IMPRINT",EDGE,{"derivedFrom":subQ2}),1.0]])]});}
            var Q49;
            {var subQ2=sQuery(id+"F0.wireOp",EDGE,"E22.left");Q49=makeQuery(id+"F0.imprint","IMPRINT",FACE,{"disambiguationData":[TD([[makeQuery(id+"F0.imprint","IMPRINT",EDGE,{"derivedFrom":subQ2}),-1.0]])]});}
            var Q50;
            {var subQ4=sQuery(id+"F0.wireOp",EDGE,"E26.top");Q50=makeQuery(id+"F0.imprint","IMPRINT",FACE,{"disambiguationData":[TD([[makeQuery(id+"F0.imprint","IMPRINT",EDGE,{"derivedFrom":subQ4}),-1.0]])]});}
            var Q51;
            {var subQ0=sQuery(id+"F0.wireOp",EDGE,"E54.bottom");Q51=makeQuery(id+"F0.imprint","IMPRINT",FACE,{"disambiguationData":[TD([[makeQuery(id+"F0.imprint","IMPRINT",EDGE,{"derivedFrom":subQ0}),1.0]])]});}
            var Q52;
            {var subQ2=sQuery(id+"F0.wireOp",EDGE,"E25.bottom");Q52=makeQuery(id+"F0.imprint","IMPRINT",FACE,{"disambiguationData":[TD([[makeQuery(id+"F0.imprint","IMPRINT",EDGE,{"derivedFrom":subQ2}),-1.0]])]});}
            var Q53;
            {var subQ0=sQuery(id+"F0.wireOp",EDGE,"E24.left");Q53=makeQuery(id+"F0.imprint","IMPRINT",FACE,{"disambiguationData":[TD([[makeQuery(id+"F0.imprint","IMPRINT",EDGE,{"derivedFrom":subQ0}),1.0]])]});}
            var Q54;
            {var subQ0=sQuery(id+"F0.wireOp",EDGE,"E19.bottom");Q54=makeQuery(id+"F0.imprint","IMPRINT",FACE,{"disambiguationData":[TD([[makeQuery(id+"F0.imprint","IMPRINT",EDGE,{"derivedFrom":subQ0}),-1.0]])]});}
            var Q55;
            {var subQ2=sQuery(id+"F0.wireOp",EDGE,"E23.bottom");Q55=makeQuery(id+"F0.imprint","IMPRINT",FACE,{"disambiguationData":[TD([[makeQuery(id+"F0.imprint","IMPRINT",EDGE,{"derivedFrom":subQ2}),1.0]])]});}
            var Q56;
            Q56=makeQuery(id+"F0.imprint","IMPRINT",FACE,{"disambiguationData":[TD([[makeQuery(id+"F0.imprint","IMPRINT",EDGE,{"derivedFrom":sQuery(id+"F0.wireOp",EDGE,"E12.bottom")}),1.0]])]});
            var Q57;
            {var subQ3=sQuery(id+"F0.wireOp",EDGE,"E53.top");Q57=makeQuery(id+"F0.imprint","IMPRINT",FACE,{"disambiguationData":[TD([[makeQuery(id+"F0.imprint","IMPRINT",EDGE,{"derivedFrom":subQ3}),1.0]])]});}
            var Q58;
            {var subQ0=sQuery(id+"F0.wireOp",EDGE,"E24.bottom");Q58=makeQuery(id+"F0.imprint","IMPRINT",FACE,{"disambiguationData":[TD([[makeQuery(id+"F0.imprint","IMPRINT",EDGE,{"derivedFrom":subQ0}),-1.0]])]});}
            var Q59;
            {var subQ4=sQuery(id+"F0.wireOp",EDGE,"E49.top");Q59=makeQuery(id+"F0.imprint","IMPRINT",FACE,{"disambiguationData":[TD([[makeQuery(id+"F0.imprint","IMPRINT",EDGE,{"derivedFrom":subQ4}),1.0]])]});}
            var Q60;
            {var subQ6=sQuery(id+"F0.wireOp",EDGE,"E47.top");Q60=makeQuery(id+"F0.imprint","IMPRINT",FACE,{"disambiguationData":[TD([[makeQuery(id+"F0.imprint","IMPRINT",EDGE,{"derivedFrom":subQ6}),1.0]])]});}
            var Q61;
            {var subQ4=sQuery(id+"F0.wireOp",EDGE,"E48.left");Q61=makeQuery(id+"F0.imprint","IMPRINT",FACE,{"disambiguationData":[TD([[makeQuery(id+"F0.imprint","IMPRINT",EDGE,{"derivedFrom":subQ4}),-1.0]])]});}
            var Q62;
            {var subQ2=sQuery(id+"F0.wireOp",EDGE,"E5.right");Q62=makeQuery(id+"F0.imprint","IMPRINT",FACE,{"disambiguationData":[TD([[makeQuery(id+"F0.imprint","IMPRINT",EDGE,{"derivedFrom":subQ2}),1.0]])]});}
            var Q63;
            {var subQ0=sQuery(id+"F0.wireOp",EDGE,"E21.left");Q63=makeQuery(id+"F0.imprint","IMPRINT",FACE,{"disambiguationData":[TD([[makeQuery(id+"F0.imprint","IMPRINT",EDGE,{"derivedFrom":subQ0}),1.0]])]});}
            var Q64;
            {var subQ0=sQuery(id+"F0.wireOp",EDGE,"E20.bottom");Q64=makeQuery(id+"F0.imprint","IMPRINT",FACE,{"disambiguationData":[TD([[makeQuery(id+"F0.imprint","IMPRINT",EDGE,{"derivedFrom":subQ0}),-1.0]])]});}
            var Q65;
            {var subQ0=sQuery(id+"F0.wireOp",EDGE,"E2.right");Q65=makeQuery(id+"F0.imprint","IMPRINT",FACE,{"disambiguationData":[TD([[makeQuery(id+"F0.imprint","IMPRINT",EDGE,{"derivedFrom":subQ0}),-1.0]])]});}
            var Q66;
            {var subQ2=sQuery(id+"F0.wireOp",EDGE,"E25.bottom");Q66=makeQuery(id+"F0.imprint","IMPRINT",FACE,{"disambiguationData":[TD([[makeQuery(id+"F0.imprint","IMPRINT",EDGE,{"derivedFrom":subQ2}),1.0]])]});}
            extrude(context, id + "F1", {"entities" : qUnion([Q0, Q1, Q2, Q3, Q4, Q5, Q6, Q7, Q8, Q9, Q10, Q11, Q12, Q13, Q14, Q15, Q16, Q17, Q18, Q19, Q20, Q21, Q22, Q23, Q24, Q25, Q26, Q27, Q28, Q29, Q30, Q31, Q32, Q33, Q34, Q35, Q36, Q37, Q38, Q39, Q40, Q41, Q42, Q43, Q44, Q45, Q46, Q47, Q48, Q49, Q50, Q51, Q52, Q53, Q54, Q55, Q56, Q57, Q58, Q59, Q60, Q61, Q62, Q63, Q64, Q65, Q66]), "depth" : 19.05 * mm, "offsetDistance" : 25.4 * mm});
        }
        {
            var Q0;
            Q0=makeQuery(id+"F0.imprint","IMPRINT",FACE,{"disambiguationData":[TD([[makeQuery(id+"F0.imprint","IMPRINT",EDGE,{"derivedFrom":sQuery(id+"F0.wireOp",EDGE,"E1.bottom")}),-1.0]])]});
            var Q1;
            {var subQ4=sQuery(id+"F0.wireOp",EDGE,"E51.bottom");Q1=makeQuery(id+"F0.imprint","IMPRINT",FACE,{"disambiguationData":[TD([[makeQuery(id+"F0.imprint","IMPRINT",EDGE,{"derivedFrom":subQ4}),-1.0]])]});}
            var Q2;
            {var subQ4=sQuery(id+"F0.wireOp",EDGE,"E49.top");Q2=makeQuery(id+"F0.imprint","IMPRINT",FACE,{"disambiguationData":[TD([[makeQuery(id+"F0.imprint","IMPRINT",EDGE,{"derivedFrom":subQ4}),1.0]])]});}
            var Q3;
            {var subQ3=sQuery(id+"F0.wireOp",EDGE,"E7.bottom");Q3=makeQuery(id+"F0.imprint","IMPRINT",FACE,{"disambiguationData":[TD([[makeQuery(id+"F0.imprint","IMPRINT",EDGE,{"derivedFrom":subQ3}),1.0]])]});}
            var Q4;
            Q4=makeQuery(id+"F0.imprint","IMPRINT",FACE,{"disambiguationData":[TD([[makeQuery(id+"F0.imprint","IMPRINT",EDGE,{"derivedFrom":sQuery(id+"F0.wireOp",EDGE,"E12.bottom")}),1.0]])]});
            var Q5;
            Q5=makeQuery(id+"F0.imprint","IMPRINT",FACE,{"disambiguationData":[TD([[makeQuery(id+"F0.imprint","IMPRINT",EDGE,{"derivedFrom":sQuery(id+"F0.wireOp",EDGE,"E5.right")}),-1.0]])]});
            var Q6;
            Q6=makeQuery(id+"F0.imprint","IMPRINT",FACE,{"disambiguationData":[TD([[makeQuery(id+"F0.imprint","IMPRINT",EDGE,{"derivedFrom":sQuery(id+"F0.wireOp",EDGE,"E6.top")}),1.0]])]});
            var Q7;
            Q7=makeQuery(id+"F0.imprint","IMPRINT",FACE,{"disambiguationData":[TD([[makeQuery(id+"F0.imprint","IMPRINT",EDGE,{"derivedFrom":sQuery(id+"F0.wireOp",EDGE,"E11.bottom")}),1.0]])]});
            var Q8;
            Q8=makeQuery(id+"F0.imprint","IMPRINT",FACE,{"disambiguationData":[TD([[makeQuery(id+"F0.imprint","IMPRINT",EDGE,{"derivedFrom":sQuery(id+"F0.wireOp",EDGE,"E9.bottom")}),1.0]])]});
            var Q9;
            {var subQ1=sQuery(id+"F0.wireOp",EDGE,"E13.top");var subQ3=sQuery(id+"F0.wireOp",EDGE,"E18.left");var subQ4=makeQuery(id+"F0.imprint","INTERSECT",VERTEX,{"derivedFrom":[subQ1,subQ3]});Q9=makeQuery(id+"F0.imprint","IMPRINT",FACE,{"disambiguationData":[TD([[makeQuery(id+"F0.imprint","IMPRINT",EDGE,{"disambiguationData":[TD([[subQ4,-1.0]])],"derivedFrom":subQ1}),1.0]])]});}
            var Q10;
            {var subQ4=sQuery(id+"F0.wireOp",EDGE,"E55.bottom");Q10=makeQuery(id+"F0.imprint","IMPRINT",FACE,{"disambiguationData":[TD([[makeQuery(id+"F0.imprint","IMPRINT",EDGE,{"derivedFrom":subQ4}),-1.0]])]});}
            var Q11;
            {var subQ4=sQuery(id+"F0.wireOp",EDGE,"E57.bottom");Q11=makeQuery(id+"F0.imprint","IMPRINT",FACE,{"disambiguationData":[TD([[makeQuery(id+"F0.imprint","IMPRINT",EDGE,{"derivedFrom":subQ4}),-1.0]])]});}
            var Q12;
            {var subQ4=sQuery(id+"F0.wireOp",EDGE,"E59.bottom");Q12=makeQuery(id+"F0.imprint","IMPRINT",FACE,{"disambiguationData":[TD([[makeQuery(id+"F0.imprint","IMPRINT",EDGE,{"derivedFrom":subQ4}),-1.0]])]});}
            var Q13;
            {var subQ4=sQuery(id+"F0.wireOp",EDGE,"E61.bottom");Q13=makeQuery(id+"F0.imprint","IMPRINT",FACE,{"disambiguationData":[TD([[makeQuery(id+"F0.imprint","IMPRINT",EDGE,{"derivedFrom":subQ4}),-1.0]])]});}
            var Q14;
            {var subQ4=sQuery(id+"F0.wireOp",EDGE,"E26.top");Q14=makeQuery(id+"F0.imprint","IMPRINT",FACE,{"disambiguationData":[TD([[makeQuery(id+"F0.imprint","IMPRINT",EDGE,{"derivedFrom":subQ4}),-1.0]])]});}
            var Q15;
            {var subQ0=sQuery(id+"F0.wireOp",EDGE,"E23.left");Q15=makeQuery(id+"F0.imprint","IMPRINT",FACE,{"disambiguationData":[TD([[makeQuery(id+"F0.imprint","IMPRINT",EDGE,{"derivedFrom":subQ0}),-1.0]])]});}
            var Q16;
            {var subQ2=sQuery(id+"F0.wireOp",EDGE,"E23.bottom");Q16=makeQuery(id+"F0.imprint","IMPRINT",FACE,{"disambiguationData":[TD([[makeQuery(id+"F0.imprint","IMPRINT",EDGE,{"derivedFrom":subQ2}),1.0]])]});}
            var Q17;
            {var subQ2=sQuery(id+"F0.wireOp",EDGE,"E21.left");Q17=makeQuery(id+"F0.imprint","IMPRINT",FACE,{"disambiguationData":[TD([[makeQuery(id+"F0.imprint","IMPRINT",EDGE,{"derivedFrom":subQ2}),-1.0]])]});}
            var Q18;
            {var subQ0=sQuery(id+"F0.wireOp",EDGE,"E21.bottom");Q18=makeQuery(id+"F0.imprint","IMPRINT",FACE,{"disambiguationData":[TD([[makeQuery(id+"F0.imprint","IMPRINT",EDGE,{"derivedFrom":subQ0}),1.0]])]});}
            var Q19;
            {var subQ0=sQuery(id+"F0.wireOp",EDGE,"E19.left");Q19=makeQuery(id+"F0.imprint","IMPRINT",FACE,{"disambiguationData":[TD([[makeQuery(id+"F0.imprint","IMPRINT",EDGE,{"derivedFrom":subQ0}),-1.0]])]});}
            var Q20;
            {var subQ0=sQuery(id+"F0.wireOp",EDGE,"E19.bottom");Q20=makeQuery(id+"F0.imprint","IMPRINT",FACE,{"disambiguationData":[TD([[makeQuery(id+"F0.imprint","IMPRINT",EDGE,{"derivedFrom":subQ0}),1.0]])]});}
            extrude(context, id + "F2", {"entities" : qUnion([Q0, Q1, Q2, Q3, Q4, Q5, Q6, Q7, Q8, Q9, Q10, Q11, Q12, Q13, Q14, Q15, Q16, Q17, Q18, Q19, Q20]), "operationType" : NewBodyOperationType.ADD, "depth" : 21.59 * mm, "offsetDistance" : 25.4 * mm});
        }
        {
            var Q0;
            {var subQ0=sQuery(id+"F0.wireOp",EDGE,"E42.bottom");var subQ1=sQuery(id+"F0.wireOp",EDGE,"E40.bottom");var subQ2=sQuery(id+"F0.wireOp",EDGE,"E37.top");var subQ3=sQuery(id+"F0.wireOp",EDGE,"E35.left");var subQ4=sQuery(id+"F0.wireOp",EDGE,"E35.top");var subQ5=sQuery(id+"F0.wireOp",EDGE,"E33.top");var subQ6=sQuery(id+"F0.wireOp",EDGE,"E27.left");var subQ7=sQuery(id+"F0.wireOp",EDGE,"E26.top");var subQ8=sQuery(id+"F0.wireOp",EDGE,"E2.left");var subQ9=sQuery(id+"F0.wireOp",EDGE,"E2.bottom");var subQ10=sQuery(id+"F0.wireOp",EDGE,"E17.left");var subQ11=sQuery(id+"F0.wireOp",EDGE,"E44.right");var subQ12=sQuery(id+"F0.wireOp",EDGE,"E44.bottom");var subQ13=sQuery(id+"F0.wireOp",EDGE,"E43.right");var subQ14=sQuery(id+"F0.wireOp",EDGE,"E43.bottom");var subQ15=sQuery(id+"F0.wireOp",EDGE,"E42.right");var subQ16=sQuery(id+"F0.wireOp",EDGE,"E41.right");var subQ17=sQuery(id+"F0.wireOp",EDGE,"E17.bottom");var subQ18=sQuery(id+"F0.wireOp",EDGE,"E16.bottom");var subQ19=sQuery(id+"F0.wireOp",EDGE,"E11.bottom");var subQ20=sQuery(id+"F0.wireOp",EDGE,"E10.right");var subQ21=sQuery(id+"F0.wireOp",EDGE,"E12.left");var subQ22=sQuery(id+"F0.wireOp",EDGE,"E8.right");var subQ23=sQuery(id+"F0.wireOp",EDGE,"E7.top");var subQ24=sQuery(id+"F0.wireOp",EDGE,"E6.right");var subQ25=sQuery(id+"F0.wireOp",EDGE,"E3.bottom");var subQ26=sQuery(id+"F0.wireOp",EDGE,"E38.right");var subQ27=sQuery(id+"F0.wireOp",EDGE,"E30.top");var subQ28=sQuery(id+"F0.wireOp",EDGE,"E16.left");var subQ29=sQuery(id+"F0.wireOp",EDGE,"E40.right");var subQ30=sQuery(id+"F0.wireOp",EDGE,"E37.left");var subQ31=sQuery(id+"F0.wireOp",EDGE,"E41.bottom");var subQ32=sQuery(id+"F0.wireOp",EDGE,"E36.left");var subQ33=sQuery(id+"F0.wireOp",EDGE,"E33.left");var subQ34=sQuery(id+"F0.wireOp",EDGE,"E39.right");var subQ35=sQuery(id+"F0.wireOp",EDGE,"E39.bottom");var subQ36=sQuery(id+"F0.wireOp",EDGE,"E38.bottom");var subQ37=sQuery(id+"F0.wireOp",EDGE,"E36.top");var subQ38=sQuery(id+"F0.wireOp",EDGE,"E34.left");var subQ39=sQuery(id+"F0.wireOp",EDGE,"E34.top");var subQ40=sQuery(id+"F0.wireOp",EDGE,"E32.left");var subQ41=sQuery(id+"F0.wireOp",EDGE,"E32.top");var subQ42=sQuery(id+"F0.wireOp",EDGE,"E31.left");var subQ43=sQuery(id+"F0.wireOp",EDGE,"E31.top");var subQ44=sQuery(id+"F0.wireOp",EDGE,"E30.left");var subQ45=sQuery(id+"F0.wireOp",EDGE,"E29.right");var subQ46=sQuery(id+"F0.wireOp",EDGE,"E29.bottom");var subQ47=sQuery(id+"F0.wireOp",EDGE,"E5.top");var subQ48=sQuery(id+"F0.wireOp",EDGE,"E4.left");var subQ49=sQuery(id+"F0.wireOp",EDGE,"E4.bottom");var subQ50=sQuery(id+"F0.wireOp",EDGE,"E3.right");var subQ51=sQuery(id+"F0.wireOp",EDGE,"E3.left");var subQ52=sQuery(id+"F0.wireOp",EDGE,"E3.top");var subQ53=makeQuery(id+"F1.opExtrude","CAP_FACE",FACE,{"disambiguationData":[OSD([sQuery(id+"F0.wireOp",EDGE,"E0.bottom"),sQuery(id+"F0.wireOp",EDGE,"E0.top"),sQuery(id+"F0.wireOp",EDGE,"E0.left"),sQuery(id+"F0.wireOp",EDGE,"E0.right"),subQ9,sQuery(id+"F0.wireOp",EDGE,"E2.top"),subQ8,sQuery(id+"F0.wireOp",EDGE,"E2.right"),subQ25,subQ52,subQ51,subQ50,subQ49,subQ48,subQ47,subQ24,subQ23,sQuery(id+"F0.wireOp",EDGE,"E7.right"),subQ22,sQuery(id+"F0.wireOp",EDGE,"E10.top"),subQ20,subQ19,sQuery(id+"F0.wireOp",EDGE,"E11.top"),sQuery(id+"F0.wireOp",EDGE,"E11.left"),sQuery(id+"F0.wireOp",EDGE,"E11.right"),sQuery(id+"F0.wireOp",EDGE,"E12.bottom"),sQuery(id+"F0.wireOp",EDGE,"E12.top"),subQ21,sQuery(id+"F0.wireOp",EDGE,"E12.right"),subQ18,subQ28,subQ17,subQ10,subQ7,sQuery(id+"F0.wireOp",EDGE,"E26.right"),sQuery(id+"F0.wireOp",EDGE,"E27.top"),subQ6,sQuery(id+"F0.wireOp",EDGE,"E28.top"),sQuery(id+"F0.wireOp",EDGE,"E28.right"),subQ46,subQ45,subQ27,subQ44,subQ43,subQ42,subQ41,subQ40,subQ5,subQ33,subQ39,subQ38,subQ4,subQ3,subQ37,subQ32,subQ2,subQ30,subQ36,subQ26,subQ35,subQ34,subQ1,subQ29,subQ31,subQ16,subQ0,subQ15,subQ14,subQ13,subQ12,subQ11])],"isStart":false});Q0=makeQuery(id+"F2.boolean.opBoolean","SPLIT",FACE,{"disambiguationData":[TD([makeQuery(id+"F1.opExtrude","SWEPT_FACE",FACE,{"disambiguationData":[OSD([subQ52])]})])],"derivedFrom":subQ53});}
            extrude(context, id + "F3", {"entities" : qUnion([Q0]), "operationType" : NewBodyOperationType.ADD, "depth" : 3.8 * mm, "offsetDistance" : 25.4 * mm});
        }
        {
            var Q0;
            Q0=sQuery(id+"F0.wireOp",VERTEX,"E62");
            var Q1;
            Q1=makeQuery(id+"F1.opExtrude","SWEPT_BODY",BODY,{"disambiguationData":[OSD([sQuery(id+"F0.wireOp",EDGE,"E0.bottom"),sQuery(id+"F0.wireOp",EDGE,"E0.top"),sQuery(id+"F0.wireOp",EDGE,"E0.left"),sQuery(id+"F0.wireOp",EDGE,"E0.right"),sQuery(id+"F0.wireOp",EDGE,"E2.bottom"),sQuery(id+"F0.wireOp",EDGE,"E2.top"),sQuery(id+"F0.wireOp",EDGE,"E2.left"),sQuery(id+"F0.wireOp",EDGE,"E2.right"),sQuery(id+"F0.wireOp",EDGE,"E3.bottom"),sQuery(id+"F0.wireOp",EDGE,"E3.top"),sQuery(id+"F0.wireOp",EDGE,"E3.left"),sQuery(id+"F0.wireOp",EDGE,"E3.right"),sQuery(id+"F0.wireOp",EDGE,"E4.bottom"),sQuery(id+"F0.wireOp",EDGE,"E4.left"),sQuery(id+"F0.wireOp",EDGE,"E5.top"),sQuery(id+"F0.wireOp",EDGE,"E6.right"),sQuery(id+"F0.wireOp",EDGE,"E7.top"),sQuery(id+"F0.wireOp",EDGE,"E7.right"),sQuery(id+"F0.wireOp",EDGE,"E8.right"),sQuery(id+"F0.wireOp",EDGE,"E10.top"),sQuery(id+"F0.wireOp",EDGE,"E10.right"),sQuery(id+"F0.wireOp",EDGE,"E11.bottom"),sQuery(id+"F0.wireOp",EDGE,"E11.top"),sQuery(id+"F0.wireOp",EDGE,"E11.left"),sQuery(id+"F0.wireOp",EDGE,"E11.right"),sQuery(id+"F0.wireOp",EDGE,"E12.bottom"),sQuery(id+"F0.wireOp",EDGE,"E12.top"),sQuery(id+"F0.wireOp",EDGE,"E12.left"),sQuery(id+"F0.wireOp",EDGE,"E12.right"),sQuery(id+"F0.wireOp",EDGE,"E16.bottom"),sQuery(id+"F0.wireOp",EDGE,"E16.left"),sQuery(id+"F0.wireOp",EDGE,"E17.bottom"),sQuery(id+"F0.wireOp",EDGE,"E17.left"),sQuery(id+"F0.wireOp",EDGE,"E26.top"),sQuery(id+"F0.wireOp",EDGE,"E26.right"),sQuery(id+"F0.wireOp",EDGE,"E27.top"),sQuery(id+"F0.wireOp",EDGE,"E27.left"),sQuery(id+"F0.wireOp",EDGE,"E28.top"),sQuery(id+"F0.wireOp",EDGE,"E28.right"),sQuery(id+"F0.wireOp",EDGE,"E29.bottom"),sQuery(id+"F0.wireOp",EDGE,"E29.right"),sQuery(id+"F0.wireOp",EDGE,"E30.top"),sQuery(id+"F0.wireOp",EDGE,"E30.left"),sQuery(id+"F0.wireOp",EDGE,"E31.top"),sQuery(id+"F0.wireOp",EDGE,"E31.left"),sQuery(id+"F0.wireOp",EDGE,"E32.top"),sQuery(id+"F0.wireOp",EDGE,"E32.left"),sQuery(id+"F0.wireOp",EDGE,"E33.top"),sQuery(id+"F0.wireOp",EDGE,"E33.left"),sQuery(id+"F0.wireOp",EDGE,"E34.top"),sQuery(id+"F0.wireOp",EDGE,"E34.left"),sQuery(id+"F0.wireOp",EDGE,"E35.top"),sQuery(id+"F0.wireOp",EDGE,"E35.left"),sQuery(id+"F0.wireOp",EDGE,"E36.top"),sQuery(id+"F0.wireOp",EDGE,"E36.left"),sQuery(id+"F0.wireOp",EDGE,"E37.top"),sQuery(id+"F0.wireOp",EDGE,"E37.left"),sQuery(id+"F0.wireOp",EDGE,"E38.bottom"),sQuery(id+"F0.wireOp",EDGE,"E38.right"),sQuery(id+"F0.wireOp",EDGE,"E39.bottom"),sQuery(id+"F0.wireOp",EDGE,"E39.right"),sQuery(id+"F0.wireOp",EDGE,"E40.bottom"),sQuery(id+"F0.wireOp",EDGE,"E40.right"),sQuery(id+"F0.wireOp",EDGE,"E41.bottom"),sQuery(id+"F0.wireOp",EDGE,"E41.right"),sQuery(id+"F0.wireOp",EDGE,"E42.bottom"),sQuery(id+"F0.wireOp",EDGE,"E42.right"),sQuery(id+"F0.wireOp",EDGE,"E43.bottom"),sQuery(id+"F0.wireOp",EDGE,"E43.right"),sQuery(id+"F0.wireOp",EDGE,"E44.bottom"),sQuery(id+"F0.wireOp",EDGE,"E44.right")])]});
            hole(context, id + "F4", {"style" : HoleStyle.SIMPLE, "endStyle" : HoleEndStyle.THROUGH, "oppositeDirection" : true, "standardTappedOrClearance" : lookupTablePath({ "fit" : "Normal (ASME)", "standard" : "ANSI", "size" : "1/4", "type" : "Clearance" }), "standardBlindInLast" : lookupTablePath({ "fit" : "Normal", "standard" : "ANSI", "size" : "1/4", "type" : "Clearance" }), "holeDiameter" : 7.14 * mm, "majorDiameter" : 6.35 * mm, "isTappedThrough" : true, "tappedDepth" : 12.7 * mm, "tapClearance" : 3, "locations" : qUnion([Q0]), "scope" : qUnion([Q1])});
        }
    });
